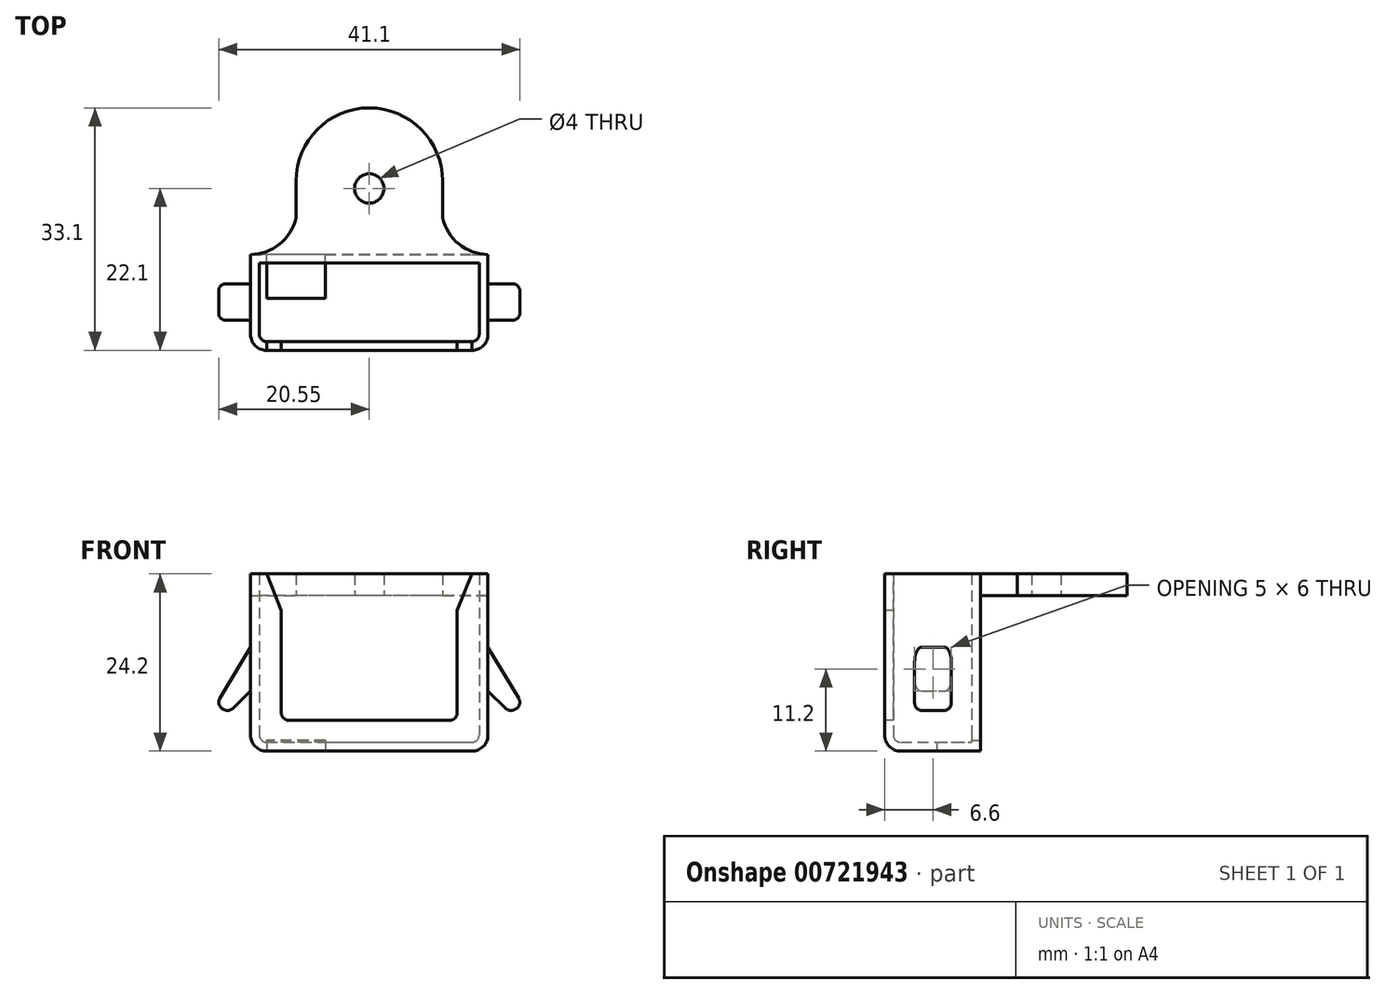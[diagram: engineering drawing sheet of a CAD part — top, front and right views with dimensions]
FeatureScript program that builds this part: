
annotation { "Feature Type Name" : "Feature", "Feature Type Description" : "" }
export const myFeature = defineFeature(function(context is Context, id is Id, definition is map)
    precondition{}
    {
        {
            var Q0;
            Q0=qCreatedBy(makeId("Front.planeOp"),FACE);
            var sketch = newSketch(context, id + "F0", { "sketchPlane" : qUnion([Q0])});
            skLineSegment(sketch, "E0.bottom", {"start": v(-15, 10) * mm, "end": v(15, 10) * mm});
            skLineSegment(sketch, "E0.top", {"start": v(-15, -20) * mm, "end": v(15, -20) * mm});
            skLineSegment(sketch, "E0.left", {"start": v(-15, 10) * mm, "end": v(-15, -20) * mm});
            skLineSegment(sketch, "E0.right", {"start": v(15, 10) * mm, "end": v(15, -20) * mm});
            skPoint(sketch, "E0.middle", {"position": v(0, -5) * mm});
            skPoint(sketch, "E1.visualSharp", {"position": v(-15, 10) * mm});
            skSolve(sketch);
        }
        {
            var Q0;
            Q0 = qSketchRegion(id + "F0", true);
            extrude(context, id + "F1", {"entities" : qUnion([Q0]), "depth" : 10.7 * mm, "offsetDistance" : 25 * mm});
        }
        {
            var Q0;
            Q0=makeQuery(id+"F1.opExtrude","SWEPT_EDGE",EDGE,{"disambiguationData":[OSD([sQuery(id+"F0.wireOp",EDGE,"E0.bottom"),sQuery(id+"F0.wireOp",EDGE,"E0.right")])]});
            var Q1;
            Q1=makeQuery(id+"F1.opExtrude","SWEPT_EDGE",EDGE,{"disambiguationData":[OSD([sQuery(id+"F0.wireOp",EDGE,"E0.bottom"),sQuery(id+"F0.wireOp",EDGE,"E0.left")])]});
            var Q2;
            Q2=makeQuery(id+"F1.opExtrude","SWEPT_EDGE",EDGE,{"disambiguationData":[OSD([sQuery(id+"F0.wireOp",EDGE,"E0.top"),sQuery(id+"F0.wireOp",EDGE,"E0.left")])]});
            var Q3;
            Q3=makeQuery(id+"F1.opExtrude","SWEPT_EDGE",EDGE,{"disambiguationData":[OSD([sQuery(id+"F0.wireOp",EDGE,"E0.top"),sQuery(id+"F0.wireOp",EDGE,"E0.right")])]});
            var Q4;
            Q4=makeQuery(id+"F1.opExtrude","CAP_FACE",FACE,{"disambiguationData":[OSD([sQuery(id+"F0.wireOp",EDGE,"E0.bottom"),sQuery(id+"F0.wireOp",EDGE,"E0.top"),sQuery(id+"F0.wireOp",EDGE,"E0.left"),sQuery(id+"F0.wireOp",EDGE,"E0.right")])],"isStart":false});
            fillet(context, id + "F2", {"entities" : qUnion([Q0, Q1, Q2, Q3, Q4]), "radius" : 1 * mm, "tangentPropagation" : true, "allowEdgeOverflow" : false});
        }
        {
            var Q0;
            Q0=makeQuery(id+"F1.opExtrude","SWEPT_FACE",FACE,{"disambiguationData":[OSD([sQuery(id+"F0.wireOp",EDGE,"E0.bottom")])]});
            var Q1;
            Q1=makeQuery(id+"F2.opFillet","BLEND_FACE",FACE,{"disambiguationData":[OSD([sQuery(id+"F0.wireOp",EDGE,"E0.bottom")])]});
            shell(context, id + "F3", {"entities" : qUnion([Q0, Q1]), "thickness" : 1.2 * mm, "oppositeDirection" : true});
        }
        {
            var Q0;
            Q0=makeQuery(id+"F1.opExtrude","CAP_FACE",FACE,{"disambiguationData":[OSD([sQuery(id+"F0.wireOp",EDGE,"E0.bottom"),sQuery(id+"F0.wireOp",EDGE,"E0.top"),sQuery(id+"F0.wireOp",EDGE,"E0.left"),sQuery(id+"F0.wireOp",EDGE,"E0.right")])],"isStart":false});
            var sketch = newSketch(context, id + "F4", { "sketchPlane" : qUnion([Q0])});
            skLineSegment(sketch, "E2.bottom", {"start": v(-11, -17) * mm, "end": v(11, -17) * mm});
            skLineSegment(sketch, "E2.top", {"start": v(-12, 15) * mm, "end": v(12, 15) * mm});
            skLineSegment(sketch, "E2.left", {"start": v(-12, -16) * mm, "end": v(-12, 15) * mm});
            skLineSegment(sketch, "E2.right", {"start": v(12, -16) * mm, "end": v(12, 15) * mm});
            skPoint(sketch, "E3.visualSharp", {"position": v(-12, -17) * mm});
            skArc(sketch, "E3.filletArc", {"start": v(-12, -16) * mm, "mid": v(-11.7, -16.7) * mm, "end": v(-11, -17) * mm});
            skPoint(sketch, "E4.visualSharp", {"position": v(12, -17) * mm});
            skArc(sketch, "E4.filletArc", {"start": v(11, -17) * mm, "mid": v(11.7, -16.7) * mm, "end": v(12, -16) * mm});
            skLineSegment(sketch, "E5.bottom", {"start": v(-16.5, 12.5) * mm, "end": v(16.5, 12.5) * mm});
            skLineSegment(sketch, "E5.top", {"start": v(-16.5, 9) * mm, "end": v(16.5, 9) * mm});
            skLineSegment(sketch, "E5.left", {"start": v(-16.5, 12.5) * mm, "end": v(-16.5, 9) * mm});
            skLineSegment(sketch, "E5.right", {"start": v(16.5, 12.5) * mm, "end": v(16.5, 9) * mm});
            skSolve(sketch);
        }
        {
            var Q0;
            Q0=makeQuery(id+"F4.imprint","IMPRINT",FACE,{"disambiguationData":[TD([[makeQuery(id+"F4.imprint","IMPRINT",EDGE,{"derivedFrom":sQuery(id+"F4.wireOp",EDGE,"E2.bottom")}),1.0]])]});
            var Q1;
            {var subQ0=sQuery(id+"F4.wireOp",EDGE,"E5.bottom");var subQ1=sQuery(id+"F4.wireOp",EDGE,"E2.left");var subQ2=makeQuery(id+"F4.imprint","INTERSECT",VERTEX,{"derivedFrom":[subQ1,subQ0]});Q1=makeQuery(id+"F4.imprint","IMPRINT",FACE,{"disambiguationData":[TD([[makeQuery(id+"F4.imprint","IMPRINT",EDGE,{"disambiguationData":[TD([[subQ2,1.0]])],"derivedFrom":subQ1}),-1.0]])]});}
            var Q2;
            {var subQ0=sQuery(id+"F4.wireOp",EDGE,"E2.top");Q2=makeQuery(id+"F4.imprint","IMPRINT",FACE,{"disambiguationData":[TD([[makeQuery(id+"F4.imprint","IMPRINT",EDGE,{"derivedFrom":subQ0}),-1.0]])]});}
            extrude(context, id + "F5", {"entities" : qUnion([Q0, Q1, Q2]), "operationType" : NewBodyOperationType.REMOVE, "oppositeDirection" : true, "depth" : 3 * mm, "offsetDistance" : 25 * mm});
        }
        {
            var Q0;
            {var subQ8=sQuery(id+"F4.wireOp",EDGE,"E5.left");Q0=makeQuery(id+"F4.imprint","IMPRINT",FACE,{"disambiguationData":[TD([[makeQuery(id+"F4.imprint","IMPRINT",EDGE,{"derivedFrom":subQ8}),1.0]])]});}
            var Q1;
            {var subQ0=sQuery(id+"F4.wireOp",EDGE,"E5.bottom");var subQ1=sQuery(id+"F4.wireOp",EDGE,"E2.left");var subQ2=makeQuery(id+"F4.imprint","INTERSECT",VERTEX,{"derivedFrom":[subQ1,subQ0]});Q1=makeQuery(id+"F4.imprint","IMPRINT",FACE,{"disambiguationData":[TD([[makeQuery(id+"F4.imprint","IMPRINT",EDGE,{"disambiguationData":[TD([[subQ2,1.0]])],"derivedFrom":subQ1}),-1.0]])]});}
            var Q2;
            {var subQ6=sQuery(id+"F4.wireOp",EDGE,"E5.right");Q2=makeQuery(id+"F4.imprint","IMPRINT",FACE,{"disambiguationData":[TD([[makeQuery(id+"F4.imprint","IMPRINT",EDGE,{"derivedFrom":subQ6}),-1.0]])]});}
            extrude(context, id + "F6", {"entities" : qUnion([Q0, Q1, Q2]), "operationType" : NewBodyOperationType.REMOVE, "oppositeDirection" : true, "depth" : 25 * mm, "offsetDistance" : 25 * mm});
        }
        {
            var Q0;
            {var subQ0=sQuery(id+"F0.wireOp",EDGE,"E0.right");var subQ1=sQuery(id+"F0.wireOp",EDGE,"E0.left");var subQ2=sQuery(id+"F0.wireOp",EDGE,"E0.top");var subQ3=sQuery(id+"F0.wireOp",EDGE,"E0.bottom");Q0=makeQuery(id+"F5.boolean.opBoolean","INTERSECT",EDGE,{"derivedFrom":[makeQuery(id+"F3.opShell","OFFSET_FACE",FACE,{"disambiguationData":[OSD([subQ3,subQ2,subQ1,subQ0]),TDD([makeQuery(id+"F2.opFillet","BLEND_EDGE",EDGE,{"blendedFrom":[makeQuery(id+"F1.opExtrude","CAP_EDGE",EDGE,{"disambiguationData":[OSD([subQ3])],"isStart":false}),makeQuery(id+"F1.opExtrude","CAP_FACE",FACE,{"disambiguationData":[OSD([subQ3,subQ2,subQ1,subQ0])],"isStart":false})],"blendedInto":[makeQuery(id+"F1.opExtrude","CAP_FACE",FACE,{"disambiguationData":[OSD([subQ3,subQ2,subQ1,subQ0])],"isStart":false})]})])]}),makeQuery(id+"F5.opExtrude","SWEPT_FACE",FACE,{"disambiguationData":[OSD([sQuery(id+"F4.wireOp",EDGE,"E2.right")])]})]});}
            var Q1;
            {var subQ0=sQuery(id+"F0.wireOp",EDGE,"E0.right");var subQ1=sQuery(id+"F0.wireOp",EDGE,"E0.left");var subQ2=sQuery(id+"F0.wireOp",EDGE,"E0.top");var subQ3=sQuery(id+"F0.wireOp",EDGE,"E0.bottom");Q1=makeQuery(id+"F5.boolean.opBoolean","INTERSECT",EDGE,{"derivedFrom":[makeQuery(id+"F3.opShell","OFFSET_FACE",FACE,{"disambiguationData":[OSD([subQ3,subQ2,subQ1,subQ0]),TDD([makeQuery(id+"F2.opFillet","BLEND_EDGE",EDGE,{"blendedFrom":[makeQuery(id+"F1.opExtrude","CAP_EDGE",EDGE,{"disambiguationData":[OSD([subQ3])],"isStart":false}),makeQuery(id+"F1.opExtrude","CAP_FACE",FACE,{"disambiguationData":[OSD([subQ3,subQ2,subQ1,subQ0])],"isStart":false})],"blendedInto":[makeQuery(id+"F1.opExtrude","CAP_FACE",FACE,{"disambiguationData":[OSD([subQ3,subQ2,subQ1,subQ0])],"isStart":false})]})])]}),makeQuery(id+"F5.opExtrude","SWEPT_FACE",FACE,{"disambiguationData":[OSD([sQuery(id+"F4.wireOp",EDGE,"E2.left")])]})]});}
            fillet(context, id + "F7", {"entities" : qUnion([Q0, Q1]), "radius" : 2 * mm, "tangentPropagation" : true, "allowEdgeOverflow" : false});
        }
        {
            var Q0;
            Q0=makeQuery(id+"F1.opExtrude","CAP_FACE",FACE,{"disambiguationData":[OSD([sQuery(id+"F0.wireOp",EDGE,"E0.bottom"),sQuery(id+"F0.wireOp",EDGE,"E0.top"),sQuery(id+"F0.wireOp",EDGE,"E0.left"),sQuery(id+"F0.wireOp",EDGE,"E0.right")])],"isStart":true});
            var sketch = newSketch(context, id + "F8", { "sketchPlane" : qUnion([Q0])});
            skLineSegment(sketch, "E6.bottom", {"start": v(6, -19.7) * mm, "end": v(14, -19.7) * mm});
            skLineSegment(sketch, "E6.top", {"start": v(6, -24.7) * mm, "end": v(14, -24.7) * mm});
            skLineSegment(sketch, "E6.left", {"start": v(6, -19.7) * mm, "end": v(6, -24.7) * mm});
            skLineSegment(sketch, "E6.right", {"start": v(14, -19.7) * mm, "end": v(14, -24.7) * mm});
            skSolve(sketch);
        }
        {
            var Q0;
            Q0 = qSketchRegion(id + "F8", true);
            extrude(context, id + "F9", {"entities" : qUnion([Q0]), "operationType" : NewBodyOperationType.REMOVE, "oppositeDirection" : true, "depth" : 6 * mm, "offsetDistance" : 25 * mm});
        }
        {
            var Q0;
            Q0=qCreatedBy(makeId("Top.planeOp"),FACE);
            var sketch = newSketch(context, id + "F10", { "sketchPlane" : qUnion([Q0])});
            skLineSegment(sketch, "E7.bottom", {"start": v(-10, 1.2) * mm, "end": v(10, 1.2) * mm});
            skLineSegment(sketch, "E7.top", {"start": v(0, 21.2) * mm, "end": v(0, 21.2) * mm});
            skLineSegment(sketch, "E7.left", {"start": v(-10, 1.2) * mm, "end": v(-10, 11.2) * mm});
            skLineSegment(sketch, "E7.right", {"start": v(10, 1.2) * mm, "end": v(10, 11.2) * mm});
            skPoint(sketch, "E8.visualSharp", {"position": v(-10, 21.2) * mm});
            skArc(sketch, "E8.filletArc", {"start": v(0, 21.2) * mm, "mid": v(-7.07, 18.27) * mm, "end": v(-10, 11.2) * mm});
            skPoint(sketch, "E9.visualSharp", {"position": v(10, 21.2) * mm});
            skArc(sketch, "E9.filletArc", {"start": v(10, 11.2) * mm, "mid": v(7.07, 18.27) * mm, "end": v(0, 21.2) * mm});
            skCircle(sketch, "E10", {"center": v(0, 10.2) * mm, "radius": 2 * mm});
            skLineSegment(sketch, "E11", {"start": v(-10, 1.2) * mm, "end": v(-16.2, 1.2) * mm});
            skLineSegment(sketch, "E12", {"start": v(10, 1.2) * mm, "end": v(16.2, 1.2) * mm});
            skArc(sketch, "E13", {"start": v(-16.2, 1.2) * mm, "mid": v(-12.22, 2.6) * mm, "end": v(-10, 6.2) * mm});
            skArc(sketch, "E14", {"start": v(10, 6.2) * mm, "mid": v(12.22, 2.6) * mm, "end": v(16.2, 1.2) * mm});
            skSolve(sketch);
        }
        {
            var Q0;
            Q0 = qSketchRegion(id + "F10", true);
            extrude(context, id + "F11", {"entities" : qUnion([Q0]), "operationType" : NewBodyOperationType.ADD, "depth" : 3 * mm, "offsetDistance" : 25 * mm});
        }
        {
            var Q0;
            Q0=makeQuery(id+"F1.opExtrude","CAP_FACE",FACE,{"disambiguationData":[OSD([sQuery(id+"F0.wireOp",EDGE,"E0.bottom"),sQuery(id+"F0.wireOp",EDGE,"E0.top"),sQuery(id+"F0.wireOp",EDGE,"E0.left"),sQuery(id+"F0.wireOp",EDGE,"E0.right")])],"isStart":true});
            var sketch = newSketch(context, id + "F12", { "sketchPlane" : qUnion([Q0])});
            skLineSegment(sketch, "E15.bottom", {"start": v(-20, 3) * mm, "end": v(20, 3) * mm});
            skLineSegment(sketch, "E15.top", {"start": v(-20, 21.77) * mm, "end": v(20, 21.77) * mm});
            skLineSegment(sketch, "E15.left", {"start": v(-20, 3) * mm, "end": v(-20, 21.77) * mm});
            skLineSegment(sketch, "E15.right", {"start": v(20, 3) * mm, "end": v(20, 21.77) * mm});
            skSolve(sketch);
        }
        {
            var Q0;
            Q0 = qSketchRegion(id + "F12", true);
            extrude(context, id + "F13", {"entities" : qUnion([Q0]), "operationType" : NewBodyOperationType.REMOVE, "oppositeDirection" : true, "depth" : 25 * mm, "offsetDistance" : 25 * mm});
        }
        {
            var Q0;
            Q0=makeQuery(id+"F13.boolean.opBoolean","INTERSECT",EDGE,{"derivedFrom":[makeQuery(id+"F5.boolean.opBoolean","COPY",FACE,{"derivedFrom":makeQuery(id+"F5.opExtrude","SWEPT_FACE",FACE,{"disambiguationData":[OSD([sQuery(id+"F4.wireOp",EDGE,"E2.right")])]})}),makeQuery(id+"F13.opExtrude","SWEPT_FACE",FACE,{"disambiguationData":[OSD([sQuery(id+"F12.wireOp",EDGE,"E15.bottom")])]})]});
            var Q1;
            Q1=makeQuery(id+"F13.boolean.opBoolean","INTERSECT",EDGE,{"derivedFrom":[makeQuery(id+"F5.boolean.opBoolean","COPY",FACE,{"derivedFrom":makeQuery(id+"F5.opExtrude","SWEPT_FACE",FACE,{"disambiguationData":[OSD([sQuery(id+"F4.wireOp",EDGE,"E2.left")])]})}),makeQuery(id+"F13.opExtrude","SWEPT_FACE",FACE,{"disambiguationData":[OSD([sQuery(id+"F12.wireOp",EDGE,"E15.bottom")])]})]});
            chamfer(context, id + "F14", {"entities" : qUnion([Q0, Q1]), "chamferType" : ChamferType.TWO_OFFSETS, "width1" : 2 * mm, "oppositeDirection" : true, "width2" : 5 * mm, "tangentPropagation" : true});
        }
        {
            var Q0;
            {var subQ2=sQuery(id+"F0.wireOp",EDGE,"E0.right");var subQ3=sQuery(id+"F0.wireOp",EDGE,"E0.top");var subQ4=sQuery(id+"F0.wireOp",EDGE,"E0.left");Q0=makeQuery(id+"F11.boolean.opBoolean","SPLIT",FACE,{"disambiguationData":[TD([makeQuery(id+"F1.opExtrude","SWEPT_FACE",FACE,{"disambiguationData":[OSD([subQ3])]})])],"derivedFrom":makeQuery(id+"F1.opExtrude","CAP_FACE",FACE,{"disambiguationData":[OSD([sQuery(id+"F0.wireOp",EDGE,"E0.bottom"),subQ3,subQ4,subQ2])],"isStart":true})});}
            var sketch = newSketch(context, id + "F15", { "sketchPlane" : qUnion([Q0])});
            skLineSegment(sketch, "E16", {"start": v(16.2, -7) * mm, "end": v(20.4, -14.03) * mm});
            skLineSegment(sketch, "E17", {"start": v(20.06, -15.4) * mm, "end": v(19.86, -15.52) * mm});
            skLineSegment(sketch, "E18", {"start": v(18.65, -15.38) * mm, "end": v(16.2, -13) * mm});
            skLineSegment(sketch, "E19", {"start": v(16.2, -13) * mm, "end": v(16.2, -7) * mm});
            skPoint(sketch, "E20.visualSharp", {"position": v(20.92, -14.9) * mm});
            skArc(sketch, "E20.filletArc", {"start": v(20.06, -15.4) * mm, "mid": v(20.52, -14.8) * mm, "end": v(20.4, -14.03) * mm});
            skPoint(sketch, "E21.visualSharp", {"position": v(19.2, -15.92) * mm});
            skArc(sketch, "E21.filletArc", {"start": v(18.65, -15.38) * mm, "mid": v(19.23, -15.66) * mm, "end": v(19.86, -15.52) * mm});
            skLineSegment(sketch, "E22.MirrorCS", {"start": v(-20.06, -15.4) * mm, "end": v(-19.86, -15.52) * mm});
            skArc(sketch, "E23.MirrorCS", {"start": v(-20.06, -15.4) * mm, "mid": v(-20.52, -14.8) * mm, "end": v(-20.4, -14.03) * mm});
            skArc(sketch, "E24.MirrorCS", {"start": v(-18.65, -15.38) * mm, "mid": v(-19.23, -15.66) * mm, "end": v(-19.86, -15.52) * mm});
            skPoint(sketch, "E25.MirrorP", {"position": v(-20.92, -14.9) * mm});
            skPoint(sketch, "E26.MirrorP", {"position": v(-19.2, -15.92) * mm});
            skLineSegment(sketch, "E27.MirrorCS", {"start": v(-16.2, -13) * mm, "end": v(-16.2, -7) * mm});
            skLineSegment(sketch, "E28.MirrorCS", {"start": v(-18.65, -15.38) * mm, "end": v(-16.2, -13) * mm});
            skLineSegment(sketch, "E29.MirrorCS", {"start": v(-16.2, -7) * mm, "end": v(-20.4, -14.03) * mm});
            skSolve(sketch);
        }
        {
            var Q0;
            Q0 = qSketchRegion(id + "F15", true);
            extrude(context, id + "F16", {"entities" : qUnion([Q0]), "operationType" : NewBodyOperationType.ADD, "oppositeDirection" : true, "depth" : 9 * mm, "offsetDistance" : 25 * mm, "hasSecondDirection" : true, "secondDirectionOppositeDirection" : true, "secondDirectionDepth" : 4 * mm});
        }
        {
            var Q0;
            Q0=makeQuery(id+"F16.opExtrude","CAP_EDGE",EDGE,{"disambiguationData":[OSD([sQuery(id+"F15.wireOp",EDGE,"E16")])],"isStart":true});
            var Q1;
            Q1=makeQuery(id+"F16.opExtrude","CAP_EDGE",EDGE,{"disambiguationData":[OSD([sQuery(id+"F15.wireOp",EDGE,"E16")])],"isStart":false});
            var Q2;
            Q2=makeQuery(id+"F16.opExtrude","CAP_EDGE",EDGE,{"disambiguationData":[OSD([sQuery(id+"F15.wireOp",EDGE,"E29.MirrorCS")])],"isStart":false});
            var Q3;
            Q3=makeQuery(id+"F16.opExtrude","CAP_EDGE",EDGE,{"disambiguationData":[OSD([sQuery(id+"F15.wireOp",EDGE,"E29.MirrorCS")])],"isStart":true});
            fillet(context, id + "F17", {"entities" : qUnion([Q0, Q1, Q2, Q3]), "radius" : 1 * mm, "tangentPropagation" : true, "allowEdgeOverflow" : false});
        }
    });
